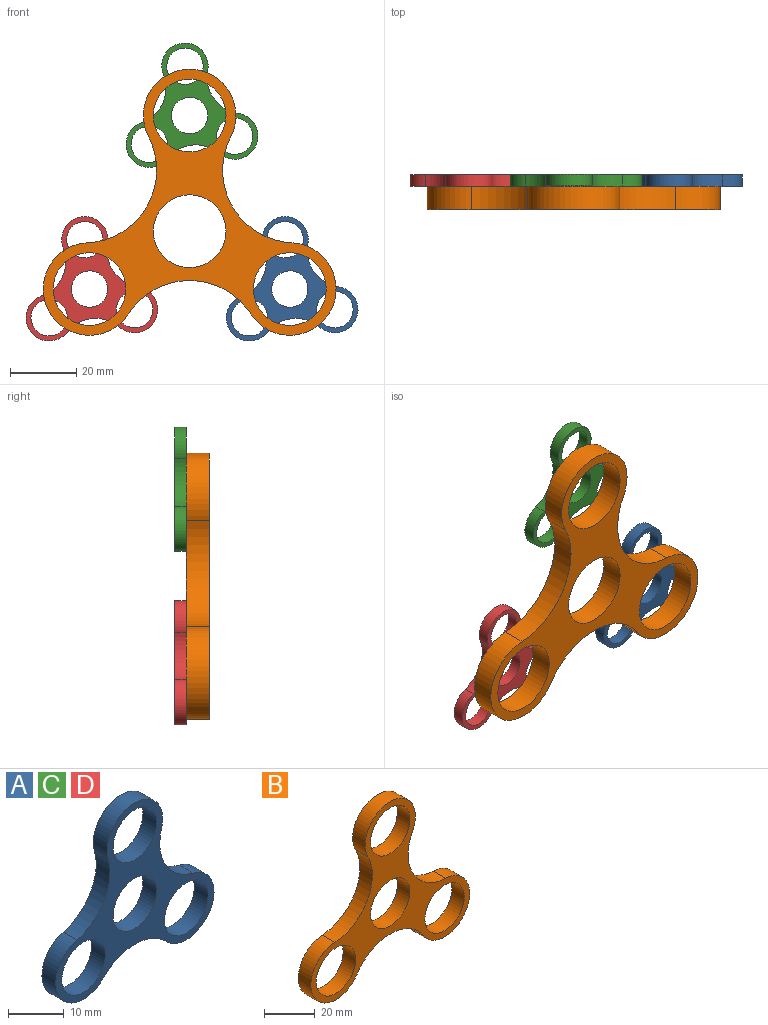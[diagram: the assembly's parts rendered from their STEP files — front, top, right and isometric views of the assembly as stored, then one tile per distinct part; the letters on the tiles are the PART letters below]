
ASSEMBLY  parts=4 mates=1
PART A: 12 faces, bbox 40x3.5x36.5 mm
  f0: cylinder r=11mm len=15.88mm, axis (0,1,0), area 62.1mm2, adj f1,f9,f10,f11
  f1: cylinder r=7mm len=13.8mm, axis (0,1,0), area 90.8mm2, adj f0,f2,f10,f11
  f2: cylinder r=11mm len=13.75mm, axis (0,1,0), area 62.1mm2, adj f1,f3,f10,f11
  f3: cylinder r=7mm len=14mm, axis (0,1,0), area 90.8mm2, adj f2,f4,f10,f11
  f4: cylinder r=11mm len=13.75mm, axis (0,1,0), area 62.1mm2, adj f3,f9,f10,f11
  f5: cylinder r=5.5mm len=11mm, axis (0,1,0), area 121mm2, adj f10,f11
  f6: cylinder r=5.5mm len=11mm, axis (0,1,0), area 121mm2, adj f10,f11
  f7: cylinder r=5.5mm len=11mm, axis (0,1,0), area 121mm2, adj f10,f11
  f8: cylinder r=5.5mm len=11mm, axis (0,1,0), area 121mm2, adj f10,f11
  f9: cylinder r=7mm len=13.8mm, axis (0,1,0), area 90.8mm2, adj f0,f4,f10,f11
  f10: plane 39.98x36.5mm, normal (0,-1,0), area 377.5mm2, adj f0,f1,f2,f3,f4,f5,f6,f7
  f11: plane 39.98x36.5mm, normal (0,1,0), area 377.5mm2, adj f0,f1,f2,f3,f4,f5,f6,f7
PART B: 12 faces, bbox 88.6x7x80.5 mm
  f0: cylinder r=22mm len=37.05mm, axis (0,1,0), area 308.3mm2, adj f1,f9,f10,f11
  f1: cylinder r=14mm len=27.99mm, axis (0,1,0), area 401.4mm2, adj f0,f2,f10,f11
  f2: cylinder r=22mm len=32.08mm, axis (0,1,0), area 308.3mm2, adj f1,f3,f10,f11
  f3: cylinder r=14mm len=28mm, axis (0,1,0), area 401.4mm2, adj f2,f4,f10,f11
  f4: cylinder r=22mm len=32.08mm, axis (0,1,0), area 308.3mm2, adj f3,f9,f10,f11
  f5: cylinder r=11mm len=22mm, axis (0,1,0), area 483.8mm2, adj f10,f11
  f6: cylinder r=11mm len=22mm, axis (0,1,0), area 483.8mm2, adj f10,f11
  f7: cylinder r=11mm len=22mm, axis (0,1,0), area 483.8mm2, adj f10,f11
  f8: cylinder r=11mm len=22mm, axis (0,1,0), area 483.8mm2, adj f10,f11
  f9: cylinder r=14mm len=27.99mm, axis (0,1,0), area 401.4mm2, adj f0,f4,f10,f11
  f10: plane 88.62x80.5mm, normal (0,-1,0), area 1587.9mm2, adj f0,f1,f2,f3,f4,f5,f6,f7
  f11: plane 88.62x80.5mm, normal (0,1,0), area 1587.9mm2, adj f0,f1,f2,f3,f4,f5,f6,f7
PART C: same geometry as A
PART D: same geometry as A
PLACE A rot(axis=(0,1,0),114.5deg) t=(33.81,-3.5,-55.17)mm
PLACE B t=(3.5,-7,-37.67)mm fixed
PLACE C rot(axis=(0,-1,0),5.5deg) t=(3.5,-3.5,-2.67)mm
PLACE D rot(axis=(0,-1,0),125.5deg) t=(-26.81,-3.5,-55.17)mm
MATE revolute C.f5 <-> B.f3  axis (0,-1,0) through (3.5,-7,-2.67)mm
